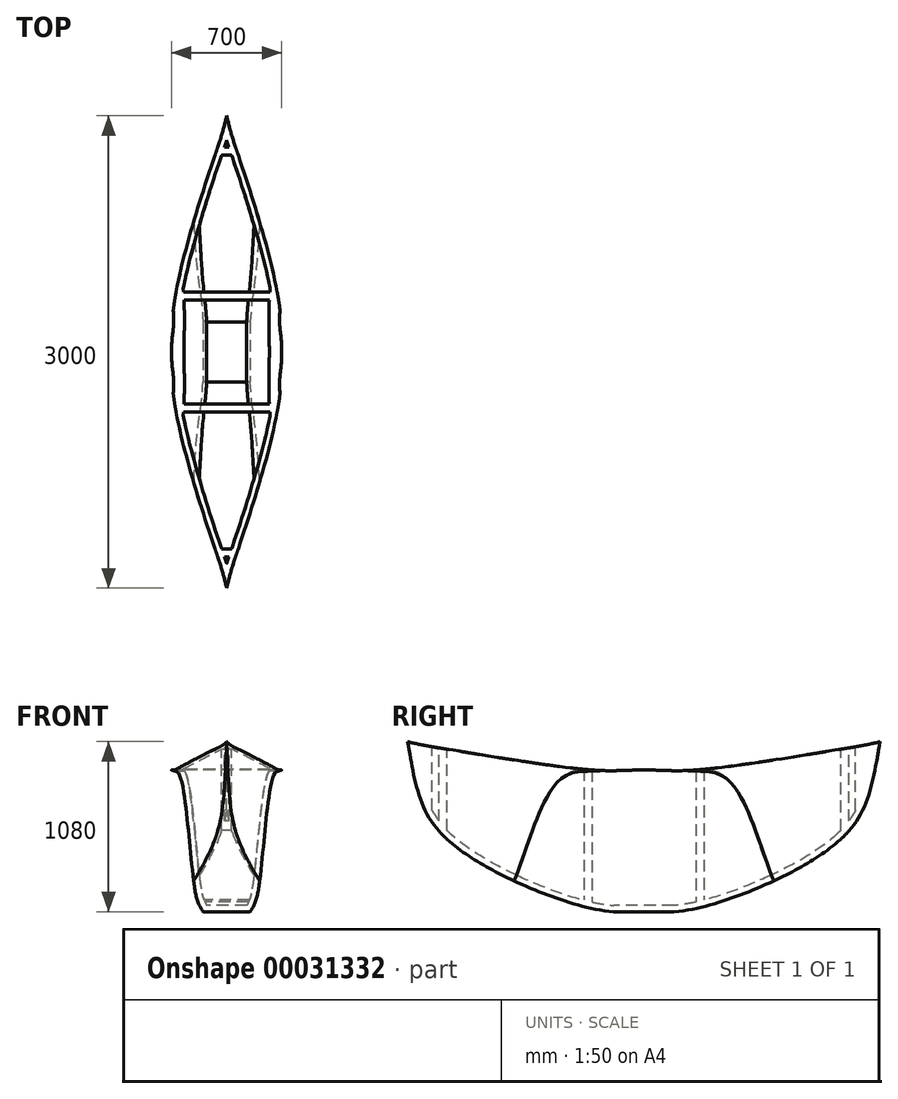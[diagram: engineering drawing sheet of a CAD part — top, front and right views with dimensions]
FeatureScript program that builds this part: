
annotation { "Feature Type Name" : "Feature", "Feature Type Description" : "" }
export const myFeature = defineFeature(function(context is Context, id is Id, definition is map)
    precondition{}
    {
        {
            var Q0;
            Q0=qCreatedBy(makeId("Front.planeOp"),FACE);
            var sketch = newSketch(context, id + "F0", { "sketchPlane" : qUnion([Q0])});
            skLineSegment(sketch, "E0.rect.bottom", {"start": v(350, 540) * mm, "end": v(-350, 540) * mm});
            skLineSegment(sketch, "E0.rect.top", {"start": v(350, -540) * mm, "end": v(-350, -540) * mm});
            skLineSegment(sketch, "E0.rect.left", {"start": v(350, 540) * mm, "end": v(350, -540) * mm});
            skLineSegment(sketch, "E0.rect.right", {"start": v(-350, 540) * mm, "end": v(-350, -540) * mm});
            skPoint(sketch, "E0.rect.middle", {"position": v(0, 0) * mm});
            skSolve(sketch);
        }
        {
            var Q0;
            Q0=makeQuery(id+"F0.imprint","IMPRINT",FACE,{"disambiguationData":[TD([[makeQuery(id+"F0.imprint","IMPRINT",EDGE,{"derivedFrom":sQuery(id+"F0.wireOp",EDGE,"E0.rect.bottom")}),1.0]])]});
            extrude(context, id + "F1", {"entities" : qUnion([Q0]), "endBound" : BoundingType.SYMMETRIC, "depth" : 3000 * mm});
        }
        {
            var Q0;
            Q0=makeQuery(id+"F1.opExtrude","SWEPT_FACE",FACE,{"disambiguationData":[OSD([sQuery(id+"F0.wireOp",EDGE,"E0.rect.right")])]});
            var sketch = newSketch(context, id + "F2", { "sketchPlane" : qUnion([Q0])});
            skFitSpline(sketch, "E1", {"points": [v(-1500, 540) * mm, v(-1250, -80) * mm, v(-330, -520) * mm, v(0, -540) * mm], "startDerivative": vector(430.17, -2486.6) * mm, "endDerivative": vector(1400.94, 0) * mm});
            skFitSpline(sketch, "E2.MirrorCS", {"points": [v(1500, 540) * mm, v(1250, -80) * mm, v(330, -520) * mm, v(0, -540) * mm], "startDerivative": vector(-430.17, -2486.6) * mm, "endDerivative": vector(-1400.94, 0) * mm});
            skFitSpline(sketch, "E3", {"points": [v(-1500, 540) * mm, v(-1250, 492) * mm, v(-330, 360) * mm, v(0, 360) * mm], "startDerivative": vector(947.9, -251.84) * mm, "endDerivative": vector(1320.88, 0) * mm});
            skFitSpline(sketch, "E4.MirrorCS", {"points": [v(1500, 540) * mm, v(1250, 492) * mm, v(330, 360) * mm, v(0, 360) * mm], "startDerivative": vector(-947.9, -251.84) * mm, "endDerivative": vector(-1320.88, 0) * mm});
            skSolve(sketch);
        }
        {
            var Q0;
            Q0=makeQuery(id+"F1.opExtrude","CAP_FACE",FACE,{"disambiguationData":[OSD([sQuery(id+"F0.wireOp",EDGE,"E0.rect.bottom"),sQuery(id+"F0.wireOp",EDGE,"E0.rect.top"),sQuery(id+"F0.wireOp",EDGE,"E0.rect.left"),sQuery(id+"F0.wireOp",EDGE,"E0.rect.right")])],"isStart":false});
            var sketch = newSketch(context, id + "F3", { "sketchPlane" : qUnion([Q0])});
            skFitSpline(sketch, "E5", {"points": [v(-350, 360) * mm, v(-300, 330) * mm, v(-200, -410) * mm, v(-150, -540) * mm], "startDerivative": vector(430.97, -176.26) * mm, "endDerivative": vector(267.8, -462.04) * mm});
            skLineSegment(sketch, "E6", {"start": v(-150, -540) * mm, "end": v(0, -540) * mm});
            skLineSegment(sketch, "E7", {"start": v(0, -540) * mm, "end": v(0, 540) * mm, "construction": true});
            skFitSpline(sketch, "E8.MirrorCS", {"points": [v(350, 360) * mm, v(300, 330) * mm, v(200, -410) * mm, v(150, -540) * mm], "startDerivative": vector(-430.97, -176.26) * mm, "endDerivative": vector(-267.8, -462.04) * mm});
            skLineSegment(sketch, "E9.MirrorCS", {"start": v(150, -540) * mm, "end": v(0, -540) * mm});
            skLineSegment(sketch, "E10", {"start": v(-350, 360) * mm, "end": v(0, 540) * mm});
            skLineSegment(sketch, "E11", {"start": v(0, 540) * mm, "end": v(350, 360) * mm});
            skSolve(sketch);
        }
        {
            var Q0;
            Q0=makeQuery(id+"F1.opExtrude","SWEPT_FACE",FACE,{"disambiguationData":[OSD([sQuery(id+"F0.wireOp",EDGE,"E0.rect.bottom")])]});
            var sketch = newSketch(context, id + "F4", { "sketchPlane" : qUnion([Q0])});
            skFitSpline(sketch, "E12", {"points": [v(0, 1500) * mm, v(-74.04, 1250) * mm, v(-330, 330) * mm, v(-350, 0) * mm], "startDerivative": vector(-355.36, -1493.98) * mm, "endDerivative": vector(-18.36, -481.25) * mm});
            skLineSegment(sketch, "E13", {"start": v(0, 0) * mm, "end": v(0, 477.53) * mm, "construction": true});
            skLineSegment(sketch, "E14", {"start": v(0, 0) * mm, "end": v(223.4, 0) * mm, "construction": true});
            skFitSpline(sketch, "E15.MirrorCS", {"points": [v(0, 1500) * mm, v(74.04, 1250) * mm, v(330, 330) * mm, v(350, 0) * mm], "startDerivative": vector(355.36, -1493.98) * mm, "endDerivative": vector(18.36, -481.25) * mm});
            skFitSpline(sketch, "E16.MirrorCS", {"points": [v(0, -1500) * mm, v(74.04, -1250) * mm, v(330, -330) * mm, v(350, 0) * mm], "startDerivative": vector(355.36, 1493.98) * mm, "endDerivative": vector(18.36, 481.25) * mm});
            skFitSpline(sketch, "E17.MirrorCS", {"points": [v(0, -1500) * mm, v(-74.04, -1250) * mm, v(-330, -330) * mm, v(-350, 0) * mm], "startDerivative": vector(-355.36, 1493.98) * mm, "endDerivative": vector(-18.36, 481.25) * mm});
            skLineSegment(sketch, "E18", {"start": v(-56.64, 1300.8) * mm, "end": v(56.64, 1300.8) * mm});
            skLineSegment(sketch, "E19", {"start": v(-74.04, 1250) * mm, "end": v(74.04, 1250) * mm});
            skLineSegment(sketch, "E20", {"start": v(-330, 330) * mm, "end": v(330, 330) * mm});
            skLineSegment(sketch, "E21", {"start": v(-321.29, 380.8) * mm, "end": v(321.29, 380.8) * mm});
            skLineSegment(sketch, "E22", {"start": v(-349.76, 25.4) * mm, "end": v(350, 25.4) * mm});
            skLineSegment(sketch, "E23.MirrorCS", {"start": v(-349.76, -25.4) * mm, "end": v(350, -25.4) * mm});
            skLineSegment(sketch, "E24.MirrorCS", {"start": v(-321.29, -380.8) * mm, "end": v(321.29, -380.8) * mm});
            skLineSegment(sketch, "E25.MirrorCS", {"start": v(-330, -330) * mm, "end": v(330, -330) * mm});
            skLineSegment(sketch, "E26.MirrorCS", {"start": v(-74.04, -1250) * mm, "end": v(74.04, -1250) * mm});
            skLineSegment(sketch, "E27.MirrorCS", {"start": v(-56.64, -1300.8) * mm, "end": v(56.64, -1300.8) * mm});
            skCircle(sketch, "E28", {"center": v(0, 0) * mm, "radius": 19.05 * mm});
            skSolve(sketch);
        }
        {
            var Q0;
            {var subQ2=sQuery(id+"F4.wireOp",EDGE,"E12");Q0=makeQuery(id+"F4.imprint","IMPRINT",FACE,{"disambiguationData":[TD([[makeQuery(id+"F4.imprint","IMPRINT",EDGE,{"derivedFrom":subQ2}),-1.0]])]});}
            var Q1;
            {var subQ2=sQuery(id+"F4.wireOp",EDGE,"E15.MirrorCS");Q1=makeQuery(id+"F4.imprint","IMPRINT",FACE,{"disambiguationData":[TD([[makeQuery(id+"F4.imprint","IMPRINT",EDGE,{"derivedFrom":subQ2}),1.0]])]});}
            var Q2;
            {var subQ2=sQuery(id+"F4.wireOp",EDGE,"E16.MirrorCS");Q2=makeQuery(id+"F4.imprint","IMPRINT",FACE,{"disambiguationData":[TD([[makeQuery(id+"F4.imprint","IMPRINT",EDGE,{"derivedFrom":subQ2}),-1.0]])]});}
            var Q3;
            {var subQ2=sQuery(id+"F4.wireOp",EDGE,"E17.MirrorCS");Q3=makeQuery(id+"F4.imprint","IMPRINT",FACE,{"disambiguationData":[TD([[makeQuery(id+"F4.imprint","IMPRINT",EDGE,{"derivedFrom":subQ2}),1.0]])]});}
            extrude(context, id + "F5", {"entities" : qUnion([Q0, Q1, Q2, Q3]), "operationType" : NewBodyOperationType.REMOVE, "endBound" : BoundingType.THROUGH_ALL, "oppositeDirection" : true, "depth" : 25.4 * mm});
        }
        {
            var Q0;
            {var subQ1=sQuery(id+"F3.wireOp",EDGE,"E10");Q0=makeQuery(id+"F3.imprint","IMPRINT",FACE,{"disambiguationData":[TD([[makeQuery(id+"F3.imprint","IMPRINT",EDGE,{"derivedFrom":subQ1}),1.0]])]});}
            var Q1;
            {var subQ1=sQuery(id+"F3.wireOp",EDGE,"E11");Q1=makeQuery(id+"F3.imprint","IMPRINT",FACE,{"disambiguationData":[TD([[makeQuery(id+"F3.imprint","IMPRINT",EDGE,{"derivedFrom":subQ1}),1.0]])]});}
            var Q2;
            {var subQ1=sQuery(id+"F3.wireOp",EDGE,"E8.MirrorCS");Q2=makeQuery(id+"F3.imprint","IMPRINT",FACE,{"disambiguationData":[TD([[makeQuery(id+"F3.imprint","IMPRINT",EDGE,{"derivedFrom":subQ1}),1.0]])]});}
            var Q3;
            {var subQ1=sQuery(id+"F3.wireOp",EDGE,"E5");Q3=makeQuery(id+"F3.imprint","IMPRINT",FACE,{"disambiguationData":[TD([[makeQuery(id+"F3.imprint","IMPRINT",EDGE,{"derivedFrom":subQ1}),-1.0]])]});}
            extrude(context, id + "F6", {"entities" : qUnion([Q0, Q1, Q2, Q3]), "operationType" : NewBodyOperationType.REMOVE, "endBound" : BoundingType.THROUGH_ALL, "oppositeDirection" : true, "depth" : 25.4 * mm});
        }
        {
            var Q0;
            Q0=makeQuery(id+"F2.imprint","IMPRINT",FACE,{"disambiguationData":[TD([[makeQuery(id+"F2.imprint","IMPRINT",EDGE,{"derivedFrom":sQuery(id+"F2.wireOp",EDGE,"E3")}),1.0]])]});
            var Q1;
            {var subQ0=sQuery(id+"F0.wireOp",EDGE,"E0.rect.right");var subQ4=makeQuery(id+"F1.opExtrude","CAP_EDGE",EDGE,{"disambiguationData":[OSD([subQ0])],"isStart":true});Q1=makeQuery(id+"F2.imprint","IMPRINT",FACE,{"disambiguationData":[TD([[makeQuery(id+"F2.imprint","IMPRINT",EDGE,{"derivedFrom":subQ4}),1.0]])]});}
            var Q2;
            {var subQ0=sQuery(id+"F0.wireOp",EDGE,"E0.rect.right");var subQ4=makeQuery(id+"F1.opExtrude","CAP_EDGE",EDGE,{"disambiguationData":[OSD([subQ0])],"isStart":false});Q2=makeQuery(id+"F2.imprint","IMPRINT",FACE,{"disambiguationData":[TD([[makeQuery(id+"F2.imprint","IMPRINT",EDGE,{"derivedFrom":subQ4}),-1.0]])]});}
            extrude(context, id + "F7", {"entities" : qUnion([Q0, Q1, Q2]), "operationType" : NewBodyOperationType.REMOVE, "endBound" : BoundingType.THROUGH_ALL, "oppositeDirection" : true, "depth" : 25.4 * mm});
        }
        {
            var Q0;
            Q0=makeQuery(id+"F7.boolean.opBoolean","COPY",FACE,{"derivedFrom":makeQuery(id+"F7.opExtrude","SWEPT_FACE",FACE,{"disambiguationData":[OSD([sQuery(id+"F2.wireOp",EDGE,"E3")])]})});
            var Q1;
            Q1=makeQuery(id+"F7.boolean.opBoolean","COPY",FACE,{"derivedFrom":makeQuery(id+"F7.opExtrude","SWEPT_FACE",FACE,{"disambiguationData":[OSD([sQuery(id+"F2.wireOp",EDGE,"E4.MirrorCS")])]})});
            shell(context, id + "F8", {"entities" : qUnion([Q0, Q1]), "thickness" : 40 * mm});
        }
        {
            var Q0;
            {var subQ2=sQuery(id+"F4.wireOp",EDGE,"E20");Q0=makeQuery(id+"F4.imprint","IMPRINT",FACE,{"disambiguationData":[TD([[makeQuery(id+"F4.imprint","IMPRINT",EDGE,{"derivedFrom":subQ2}),1.0]])]});}
            extrude(context, id + "F9", {"entities" : qUnion([Q0]), "operationType" : NewBodyOperationType.ADD, "endBound" : BoundingType.UP_TO_NEXT, "oppositeDirection" : true, "depth" : 25.4 * mm});
        }
        {
            var Q0;
            {var subQ1=sQuery(id+"F4.wireOp",EDGE,"E24.MirrorCS");Q0=makeQuery(id+"F4.imprint","IMPRINT",FACE,{"disambiguationData":[TD([[makeQuery(id+"F4.imprint","IMPRINT",EDGE,{"derivedFrom":subQ1}),1.0]])]});}
            extrude(context, id + "F10", {"entities" : qUnion([Q0]), "operationType" : NewBodyOperationType.ADD, "endBound" : BoundingType.UP_TO_NEXT, "oppositeDirection" : true, "depth" : 25.4 * mm});
        }
        {
            var Q0;
            {var subQ2=sQuery(id+"F4.wireOp",EDGE,"E18");Q0=makeQuery(id+"F4.imprint","IMPRINT",FACE,{"disambiguationData":[TD([[makeQuery(id+"F4.imprint","IMPRINT",EDGE,{"derivedFrom":subQ2}),-1.0]])]});}
            extrude(context, id + "F11", {"entities" : qUnion([Q0]), "operationType" : NewBodyOperationType.ADD, "endBound" : BoundingType.UP_TO_NEXT, "oppositeDirection" : true, "depth" : 25.4 * mm});
        }
        {
            var Q0;
            {var subQ1=sQuery(id+"F4.wireOp",EDGE,"E26.MirrorCS");Q0=makeQuery(id+"F4.imprint","IMPRINT",FACE,{"disambiguationData":[TD([[makeQuery(id+"F4.imprint","IMPRINT",EDGE,{"derivedFrom":subQ1}),-1.0]])]});}
            extrude(context, id + "F12", {"entities" : qUnion([Q0]), "operationType" : NewBodyOperationType.ADD, "endBound" : BoundingType.UP_TO_NEXT, "oppositeDirection" : true, "depth" : 25.4 * mm});
        }
        {
            var Q0;
            {var subQ1=sQuery(id+"F3.wireOp",EDGE,"E10");Q0=makeQuery(id+"F3.imprint","IMPRINT",FACE,{"disambiguationData":[TD([[makeQuery(id+"F3.imprint","IMPRINT",EDGE,{"derivedFrom":subQ1}),1.0]])]});}
            var Q1;
            {var subQ1=sQuery(id+"F3.wireOp",EDGE,"E11");Q1=makeQuery(id+"F3.imprint","IMPRINT",FACE,{"disambiguationData":[TD([[makeQuery(id+"F3.imprint","IMPRINT",EDGE,{"derivedFrom":subQ1}),1.0]])]});}
            extrude(context, id + "F13", {"entities" : qUnion([Q0, Q1]), "operationType" : NewBodyOperationType.REMOVE, "endBound" : BoundingType.THROUGH_ALL, "oppositeDirection" : true, "depth" : 25.4 * mm});
        }
        {
            var Q0;
            {var subQ6=sQuery(id+"F4.wireOp",EDGE,"E12");var subQ10=sQuery(id+"F4.wireOp",EDGE,"E22");var subQ12=makeQuery(id+"F4.imprint","INTERSECT",VERTEX,{"derivedFrom":[subQ6,subQ10]});Q0=makeQuery(id+"F4.imprint","IMPRINT",FACE,{"disambiguationData":[TD([[makeQuery(id+"F4.imprint","IMPRINT",EDGE,{"disambiguationData":[TD([[subQ12,-1.0]])],"derivedFrom":subQ10}),-1.0]])]});}
            extrude(context, id + "F14", {"entities" : qUnion([Q0]), "oppositeDirection" : true, "depth" : 1079.5 * mm});
        }
        {
            var Q0;
            {var subQ1=sQuery(id+"F3.wireOp",EDGE,"E5");Q0=makeQuery(id+"F3.imprint","IMPRINT",FACE,{"disambiguationData":[TD([[makeQuery(id+"F3.imprint","IMPRINT",EDGE,{"derivedFrom":subQ1}),-1.0]])]});}
            var Q1;
            {var subQ1=sQuery(id+"F3.wireOp",EDGE,"E8.MirrorCS");Q1=makeQuery(id+"F3.imprint","IMPRINT",FACE,{"disambiguationData":[TD([[makeQuery(id+"F3.imprint","IMPRINT",EDGE,{"derivedFrom":subQ1}),1.0]])]});}
            var Q2;
            {var subQ1=sQuery(id+"F3.wireOp",EDGE,"E11");Q2=makeQuery(id+"F3.imprint","IMPRINT",FACE,{"disambiguationData":[TD([[makeQuery(id+"F3.imprint","IMPRINT",EDGE,{"derivedFrom":subQ1}),1.0]])]});}
            var Q3;
            {var subQ1=sQuery(id+"F3.wireOp",EDGE,"E10");Q3=makeQuery(id+"F3.imprint","IMPRINT",FACE,{"disambiguationData":[TD([[makeQuery(id+"F3.imprint","IMPRINT",EDGE,{"derivedFrom":subQ1}),1.0]])]});}
            extrude(context, id + "F15", {"entities" : qUnion([Q0, Q1, Q2, Q3]), "operationType" : NewBodyOperationType.REMOVE, "endBound" : BoundingType.THROUGH_ALL, "oppositeDirection" : true, "depth" : 25.4 * mm});
        }
        {
            var Q0;
            Q0=makeQuery(id+"F2.imprint","IMPRINT",FACE,{"disambiguationData":[TD([[makeQuery(id+"F2.imprint","IMPRINT",EDGE,{"derivedFrom":sQuery(id+"F2.wireOp",EDGE,"E3")}),1.0]])]});
            extrude(context, id + "F16", {"entities" : qUnion([Q0]), "operationType" : NewBodyOperationType.REMOVE, "endBound" : BoundingType.THROUGH_ALL, "oppositeDirection" : true, "depth" : 25.4 * mm});
        }
    });
